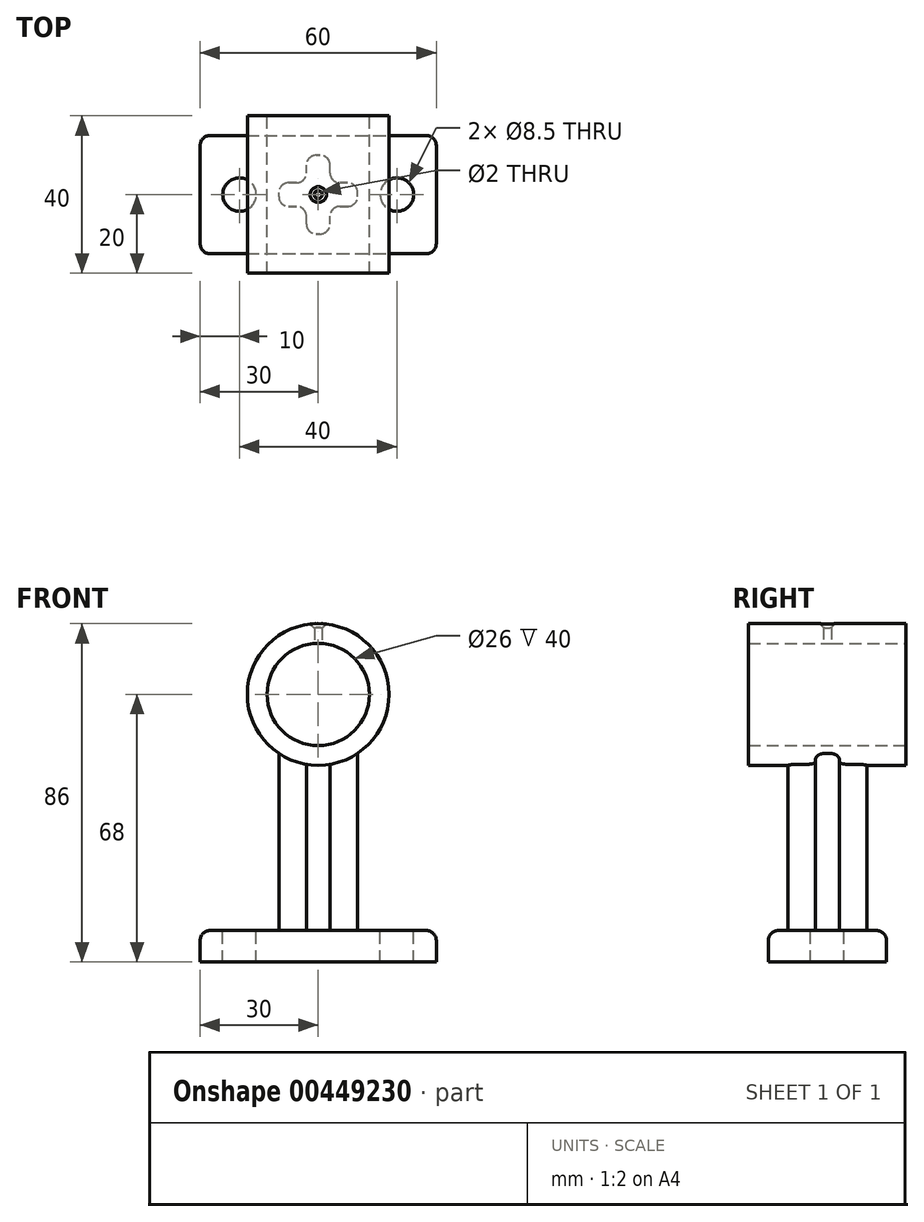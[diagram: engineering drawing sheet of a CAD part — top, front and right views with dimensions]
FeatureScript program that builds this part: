
annotation { "Feature Type Name" : "Feature", "Feature Type Description" : "" }
export const myFeature = defineFeature(function(context is Context, id is Id, definition is map)
    precondition{}
    {
        {
            var Q0;
            Q0=qCreatedBy(makeId("Front.planeOp"),FACE);
            var sketch = newSketch(context, id + "F0", { "sketchPlane" : qUnion([Q0])});
            skCircle(sketch, "E0", {"center": v(0, 0) * mm, "radius": 18 * mm});
            skCircle(sketch, "E1", {"center": v(0, 0) * mm, "radius": 13 * mm});
            skLineSegment(sketch, "E2", {"start": v(0, 0) * mm, "end": v(0, -30.22) * mm, "construction": true});
            skLineSegment(sketch, "E3.bottom", {"start": v(-30, -60) * mm, "end": v(30, -60) * mm});
            skLineSegment(sketch, "E3.top", {"start": v(-30, -68) * mm, "end": v(30, -68) * mm});
            skLineSegment(sketch, "E3.left", {"start": v(-30, -60) * mm, "end": v(-30, -68) * mm});
            skLineSegment(sketch, "E3.right", {"start": v(30, -60) * mm, "end": v(30, -68) * mm});
            skSolve(sketch);
        }
        {
            var Q0;
            Q0=makeQuery(id+"F0.imprint","IMPRINT",FACE,{"disambiguationData":[TD([[makeQuery(id+"F0.imprint","IMPRINT",EDGE,{"derivedFrom":sQuery(id+"F0.wireOp",EDGE,"E0")}),1.0]])]});
            extrude(context, id + "F1", {"entities" : qUnion([Q0]), "depth" : 40 * mm, "symmetric" : true});
        }
        {
            var Q0;
            Q0=makeQuery(id+"F0.imprint","IMPRINT",FACE,{"disambiguationData":[TD([[makeQuery(id+"F0.imprint","IMPRINT",EDGE,{"derivedFrom":sQuery(id+"F0.wireOp",EDGE,"E3.bottom")}),-1.0]])]});
            extrude(context, id + "F2", {"entities" : qUnion([Q0]), "depth" : 30 * mm, "symmetric" : true});
        }
        {
            var Q0;
            Q0=makeQuery(id+"F2.opExtrude","SWEPT_FACE",FACE,{"disambiguationData":[OSD([sQuery(id+"F0.wireOp",EDGE,"E3.bottom")])]});
            var sketch = newSketch(context, id + "F3", { "sketchPlane" : qUnion([Q0])});
            skLineSegment(sketch, "E4", {"start": v(0, 0) * mm, "end": v(-20, 0) * mm, "construction": true});
            skLineSegment(sketch, "E5", {"start": v(0, 0) * mm, "end": v(0, 10.45) * mm, "construction": true});
            skPoint(sketch, "E6", {"position": v(-20, 0) * mm});
            skPoint(sketch, "E7.MirrorP", {"position": v(20, 0) * mm});
            skLineSegment(sketch, "E8.bottom", {"start": v(7.5, 3) * mm, "end": v(5.5, 3) * mm});
            skLineSegment(sketch, "E8.top", {"start": v(7.5, -3) * mm, "end": v(5.5, -3) * mm});
            skLineSegment(sketch, "E8.left", {"start": v(10, 0.5) * mm, "end": v(10, -0.5) * mm});
            skLineSegment(sketch, "E8.right", {"start": v(-10, 0.5) * mm, "end": v(-10, -0.5) * mm});
            skPoint(sketch, "E8.middle", {"position": v(0, 0) * mm});
            skLineSegment(sketch, "E9.bottom", {"start": v(0.5, 10) * mm, "end": v(-0.5, 10) * mm});
            skLineSegment(sketch, "E9.top", {"start": v(0.5, -10) * mm, "end": v(-0.5, -10) * mm});
            skLineSegment(sketch, "E9.left", {"start": v(3, 7.5) * mm, "end": v(3, 5.5) * mm});
            skLineSegment(sketch, "E9.right", {"start": v(-3, 7.5) * mm, "end": v(-3, 5.5) * mm});
            skLineSegment(sketch, "E10.trimOffspring", {"start": v(-5.5, 3) * mm, "end": v(-7.5, 3) * mm});
            skLineSegment(sketch, "E11.trimOffspring", {"start": v(-3, -5.5) * mm, "end": v(-3, -7.5) * mm});
            skLineSegment(sketch, "E12.trimOffspring", {"start": v(-5.5, -3) * mm, "end": v(-7.5, -3) * mm});
            skLineSegment(sketch, "E13.trimOffspring", {"start": v(3, -5.5) * mm, "end": v(3, -7.5) * mm});
            skPoint(sketch, "E14.visualSharp", {"position": v(-3, 10) * mm});
            skArc(sketch, "E14.filletArc", {"start": v(-0.5, 10) * mm, "mid": v(-2.27, 9.27) * mm, "end": v(-3, 7.5) * mm});
            skPoint(sketch, "E15.visualSharp", {"position": v(3, 10) * mm});
            skArc(sketch, "E15.filletArc", {"start": v(3, 7.5) * mm, "mid": v(2.27, 9.27) * mm, "end": v(0.5, 10) * mm});
            skPoint(sketch, "E16.visualSharp", {"position": v(10, 3) * mm});
            skArc(sketch, "E16.filletArc", {"start": v(8.84, 2.6) * mm, "mid": v(8.2, 2.9) * mm, "end": v(7.5, 3) * mm});
            skPoint(sketch, "E17.visualSharp", {"position": v(10, 0.5) * mm});
            skArc(sketch, "E17.filletArc", {"start": v(10, 0.5) * mm, "mid": v(9.7, 1.7) * mm, "end": v(8.84, 2.6) * mm});
            skPoint(sketch, "E18.visualSharp", {"position": v(3, -3) * mm});
            skArc(sketch, "E18.filletArc", {"start": v(5.5, -3) * mm, "mid": v(3.73, -3.73) * mm, "end": v(3, -5.5) * mm});
            skPoint(sketch, "E19.visualSharp", {"position": v(3, -10) * mm});
            skArc(sketch, "E19.filletArc", {"start": v(0.5, -10) * mm, "mid": v(2.27, -9.27) * mm, "end": v(3, -7.5) * mm});
            skPoint(sketch, "E20.visualSharp", {"position": v(-3, -10) * mm});
            skArc(sketch, "E20.filletArc", {"start": v(-3, -7.5) * mm, "mid": v(-2.27, -9.27) * mm, "end": v(-0.5, -10) * mm});
            skPoint(sketch, "E21.visualSharp", {"position": v(-3, -3) * mm});
            skArc(sketch, "E21.filletArc", {"start": v(-3, -5.5) * mm, "mid": v(-3.73, -3.73) * mm, "end": v(-5.5, -3) * mm});
            skPoint(sketch, "E22.visualSharp", {"position": v(3, 3) * mm});
            skArc(sketch, "E22.filletArc", {"start": v(3, 5.5) * mm, "mid": v(3.73, 3.73) * mm, "end": v(5.5, 3) * mm});
            skPoint(sketch, "E23.visualSharp", {"position": v(-10, -3) * mm});
            skArc(sketch, "E23.filletArc", {"start": v(-10, -0.5) * mm, "mid": v(-9.27, -2.27) * mm, "end": v(-7.5, -3) * mm});
            skPoint(sketch, "E24.visualSharp", {"position": v(-10, 3) * mm});
            skArc(sketch, "E24.filletArc", {"start": v(-7.5, 3) * mm, "mid": v(-9.27, 2.27) * mm, "end": v(-10, 0.5) * mm});
            skPoint(sketch, "E25.visualSharp", {"position": v(-3, 3) * mm});
            skArc(sketch, "E25.filletArc", {"start": v(-5.5, 3) * mm, "mid": v(-3.73, 3.73) * mm, "end": v(-3, 5.5) * mm});
            skPoint(sketch, "E26.visualSharp", {"position": v(10, -3) * mm});
            skArc(sketch, "E26.filletArc", {"start": v(7.5, -3) * mm, "mid": v(9.27, -2.27) * mm, "end": v(10, -0.5) * mm});
            skSolve(sketch);
        }
        {
            var Q0;
            Q0 = qSketchRegion(id + "F3", true);
            extrude(context, id + "F4", {"entities" : qUnion([Q0]), "operationType" : NewBodyOperationType.ADD, "endBound" : BoundingType.UP_TO_NEXT, "depth" : 25 * mm});
        }
        {
            var Q0;
            Q0=sQuery(id+"F3.wireOp",VERTEX,"E6");
            var Q1;
            Q1=sQuery(id+"F3.wireOp",VERTEX,"E7.MirrorP");
            var Q2;
            Q2=makeQuery(id+"F1.opExtrude","SWEPT_BODY",BODY,{"disambiguationData":[OSD([sQuery(id+"F0.wireOp",EDGE,"E0"),sQuery(id+"F0.wireOp",EDGE,"E1")])]});
            hole(context, id + "F5", {"style" : HoleStyle.SIMPLE, "endStyle" : HoleEndStyle.THROUGH, "holeDiameter" : 8.5 * mm, "tappedDepth" : 12 * mm, "tapClearance" : 3, "startFromSketch" : true, "locations" : qUnion([Q0, Q1]), "scope" : qUnion([Q2])});
        }
        {
            var Q0;
            Q0=qCreatedBy(makeId("Top.planeOp"),FACE);
            var sketch = newSketch(context, id + "F6", { "sketchPlane" : qUnion([Q0])});
            skCircle(sketch, "E27", {"center": v(0, 0) * mm, "radius": 1 * mm});
            skSolve(sketch);
        }
        {
            var Q0;
            Q0 = qSketchRegion(id + "F6", true);
            extrude(context, id + "F7", {"entities" : qUnion([Q0]), "operationType" : NewBodyOperationType.REMOVE, "endBound" : BoundingType.THROUGH_ALL, "depth" : 25 * mm});
        }
        {
            var Q0;
            Q0=makeQuery(id+"F7.boolean.opBoolean","INTERSECT",EDGE,{"derivedFrom":[makeQuery(id+"F1.opExtrude","SWEPT_FACE",FACE,{"disambiguationData":[OSD([sQuery(id+"F0.wireOp",EDGE,"E0")])]}),makeQuery(id+"F7.opExtrude","SWEPT_FACE",FACE,{"disambiguationData":[OSD([sQuery(id+"F6.wireOp",EDGE,"E27")])]})]});
            chamfer(context, id + "F8", {"entities" : qUnion([Q0]), "width" : 1 * mm, "tangentPropagation" : true});
        }
        {
            var Q0;
            Q0=makeQuery(id+"F2.opExtrude","CAP_EDGE",EDGE,{"disambiguationData":[OSD([sQuery(id+"F0.wireOp",EDGE,"E3.right")])],"isStart":false});
            var Q1;
            Q1=makeQuery(id+"F2.opExtrude","CAP_EDGE",EDGE,{"disambiguationData":[OSD([sQuery(id+"F0.wireOp",EDGE,"E3.right")])],"isStart":true});
            var Q2;
            Q2=makeQuery(id+"F2.opExtrude","CAP_EDGE",EDGE,{"disambiguationData":[OSD([sQuery(id+"F0.wireOp",EDGE,"E3.left")])],"isStart":false});
            var Q3;
            Q3=makeQuery(id+"F4.opExtrude","CAP_EDGE",EDGE,{"disambiguationData":[OSD([sQuery(id+"F3.wireOp",EDGE,"E18.filletArc")])],"isStart":true});
            var Q4;
            Q4=makeQuery(id+"F2.opExtrude","CAP_EDGE",EDGE,{"disambiguationData":[OSD([sQuery(id+"F0.wireOp",EDGE,"E3.left")])],"isStart":true});
            var Q5;
            Q5=makeQuery(id+"F4.opExtrude","CAP_EDGE",EDGE,{"disambiguationData":[OSD([sQuery(id+"F3.wireOp",EDGE,"E18.filletArc")])],"isStart":false});
            fillet(context, id + "F9", {"entities" : qUnion([Q0, Q1, Q2, Q3, Q4, Q5]), "radius" : 2.5 * mm, "tangentPropagation" : true, "allowEdgeOverflow" : false});
        }
        {
            var Q0;
            Q0=makeQuery(id+"F2.opExtrude","CAP_EDGE",EDGE,{"disambiguationData":[OSD([sQuery(id+"F0.wireOp",EDGE,"E3.bottom")])],"isStart":false});
            fillet(context, id + "F10", {"entities" : qUnion([Q0]), "radius" : 2.5 * mm, "tangentPropagation" : true, "allowEdgeOverflow" : false});
        }
    });
